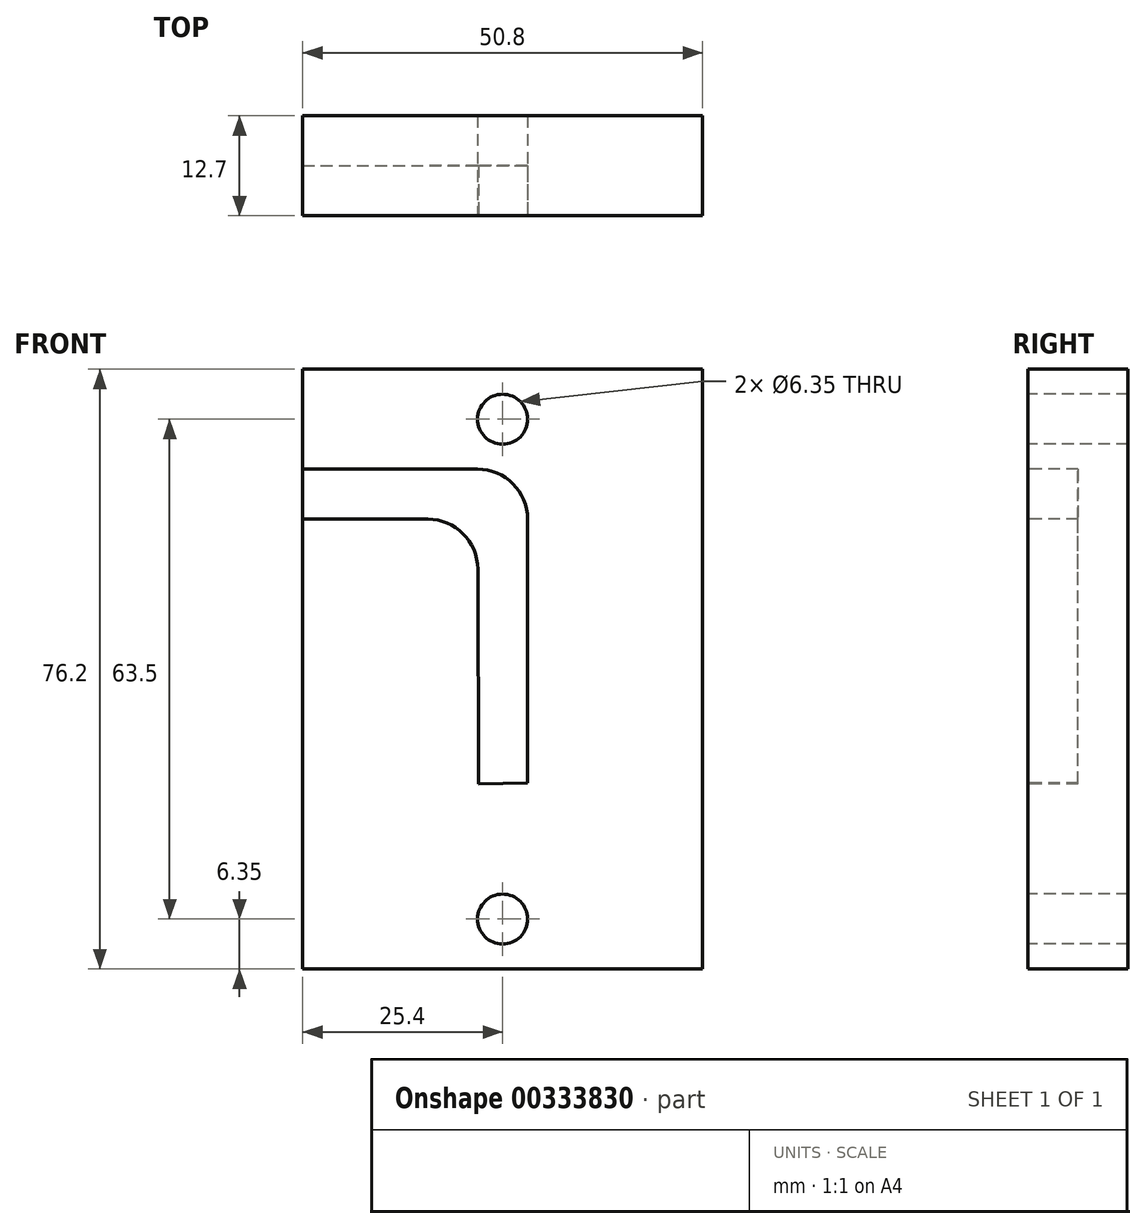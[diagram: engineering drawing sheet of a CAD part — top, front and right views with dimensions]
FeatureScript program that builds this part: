
annotation { "Feature Type Name" : "Feature", "Feature Type Description" : "" }
export const myFeature = defineFeature(function(context is Context, id is Id, definition is map)
    precondition{}
    {
        {
            var Q0;
            Q0=qCreatedBy(makeId("Front.planeOp"),FACE);
            var sketch = newSketch(context, id + "F0", { "sketchPlane" : qUnion([Q0])});
            skLineSegment(sketch, "E0", {"start": v(0, 0) * mm, "end": v(50.8, 0) * mm});
            skLineSegment(sketch, "E1", {"start": v(50.8, 0) * mm, "end": v(50.8, 76.2) * mm});
            skLineSegment(sketch, "E2", {"start": v(50.8, 76.2) * mm, "end": v(0, 76.2) * mm});
            skLineSegment(sketch, "E3", {"start": v(0, 76.2) * mm, "end": v(0, 0) * mm});
            skSolve(sketch);
        }
        {
            var Q0;
            Q0 = qSketchRegion(id + "F0", true);
            extrude(context, id + "F1", {"entities" : qUnion([Q0]), "depth" : 12.7 * mm});
        }
        {
            var Q0;
            Q0=makeQuery(id+"F1.opExtrude","CAP_FACE",FACE,{"disambiguationData":[OSD([sQuery(id+"F0.wireOp",EDGE,"E0"),sQuery(id+"F0.wireOp",EDGE,"E1"),sQuery(id+"F0.wireOp",EDGE,"E2"),sQuery(id+"F0.wireOp",EDGE,"E3")])],"isStart":false});
            var sketch = newSketch(context, id + "F2", { "sketchPlane" : qUnion([Q0])});
            skLineSegment(sketch, "E4.bottom", {"start": v(0, 63.5) * mm, "end": v(22.23, 63.5) * mm});
            skLineSegment(sketch, "E4.top", {"start": v(0, 57.15) * mm, "end": v(15.9, 57.15) * mm});
            skLineSegment(sketch, "E4.left", {"start": v(0, 63.5) * mm, "end": v(0, 57.15) * mm});
            skLineSegment(sketch, "E5", {"start": v(28.58, 23.61) * mm, "end": v(28.58, 57.15) * mm});
            skLineSegment(sketch, "E6", {"start": v(22.34, 23.5) * mm, "end": v(22.25, 50.82) * mm});
            skLineSegment(sketch, "E7", {"start": v(22.34, 23.5) * mm, "end": v(28.58, 23.61) * mm});
            skPoint(sketch, "E8.visualSharp", {"position": v(28.57, 63.5) * mm});
            skArc(sketch, "E8.filletArc", {"start": v(28.57, 57.15) * mm, "mid": v(26.72, 61.64) * mm, "end": v(22.23, 63.5) * mm});
            skPoint(sketch, "E9.visualSharp", {"position": v(22.22, 57.15) * mm});
            skArc(sketch, "E9.filletArc", {"start": v(22.25, 50.82) * mm, "mid": v(20.38, 55.3) * mm, "end": v(15.9, 57.15) * mm});
            skSolve(sketch);
        }
        {
            var Q0;
            Q0 = qSketchRegion(id + "F2", true);
            extrude(context, id + "F3", {"entities" : qUnion([Q0]), "operationType" : NewBodyOperationType.REMOVE, "oppositeDirection" : true, "depth" : 6.35 * mm});
        }
        {
            var Q0;
            Q0=makeQuery(id+"F1.opExtrude","CAP_FACE",FACE,{"disambiguationData":[OSD([sQuery(id+"F0.wireOp",EDGE,"E0"),sQuery(id+"F0.wireOp",EDGE,"E1"),sQuery(id+"F0.wireOp",EDGE,"E2"),sQuery(id+"F0.wireOp",EDGE,"E3")])],"isStart":false});
            var sketch = newSketch(context, id + "F4", { "sketchPlane" : qUnion([Q0])});
            skCircle(sketch, "E10", {"center": v(25.4, 69.85) * mm, "radius": 3.18 * mm});
            skCircle(sketch, "E11", {"center": v(25.4, 6.35) * mm, "radius": 3.18 * mm});
            skPoint(sketch, "E12", {"position": v(25.4, 0) * mm});
            skSolve(sketch);
        }
        {
            var Q0;
            Q0 = qSketchRegion(id + "F4", true);
            extrude(context, id + "F5", {"entities" : qUnion([Q0]), "operationType" : NewBodyOperationType.REMOVE, "endBound" : BoundingType.THROUGH_ALL, "oppositeDirection" : true, "depth" : 25.4 * mm});
        }
    });
